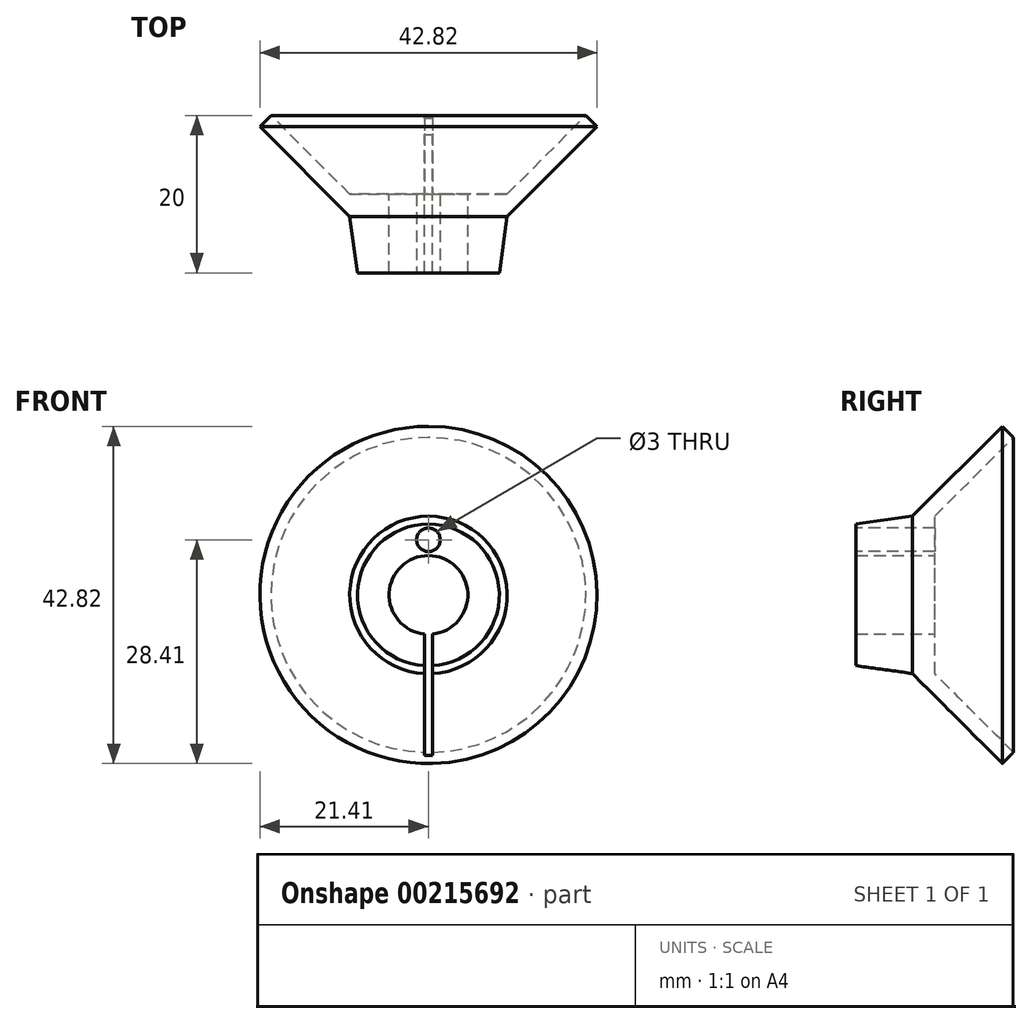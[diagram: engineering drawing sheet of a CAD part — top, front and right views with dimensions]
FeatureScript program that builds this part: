
annotation { "Feature Type Name" : "Feature", "Feature Type Description" : "" }
export const myFeature = defineFeature(function(context is Context, id is Id, definition is map)
    precondition{}
    {
        {
            var Q0;
            Q0=qCreatedBy(makeId("Top.planeOp"),FACE);
            var sketch = newSketch(context, id + "F0", { "sketchPlane" : qUnion([Q0])});
            skLineSegment(sketch, "E0", {"start": v(0, 36.3) * mm, "end": v(0, -39) * mm, "construction": true});
            skLineSegment(sketch, "E1", {"start": v(-20, 20) * mm, "end": v(-21.41, 18.59) * mm});
            skLineSegment(sketch, "E2", {"start": v(-21.41, 18.59) * mm, "end": v(-10, 7.17) * mm});
            skLineSegment(sketch, "E3", {"start": v(-5, 0) * mm, "end": v(-5, 10) * mm});
            skLineSegment(sketch, "E4", {"start": v(-10, 7.17) * mm, "end": v(-9, 0) * mm});
            skLineSegment(sketch, "E5", {"start": v(-9, 0) * mm, "end": v(-5, 0) * mm});
            skLineSegment(sketch, "E6", {"start": v(-5, 10) * mm, "end": v(-10, 10) * mm});
            skLineSegment(sketch, "E7", {"start": v(-10, 10) * mm, "end": v(-20, 20) * mm});
            skSolve(sketch);
        }
        {
            var Q0;
            Q0 = qSketchRegion(id + "F0", true);
            var Q1;
            Q1=sQuery(id+"F0.wireOp",EDGE,"E0");
            revolve(context, id + "F1", {"entities" : qUnion([Q0]), "axis" : qUnion([Q1]), "revolveType" : RevolveType.FULL});
        }
        {
            var Q0;
            Q0=makeQuery(id+"F1.opRevolve","SWEPT_FACE",FACE,{"disambiguationData":[OSD([sQuery(id+"F0.wireOp",EDGE,"E5")])]});
            var sketch = newSketch(context, id + "F2", { "sketchPlane" : qUnion([Q0])});
            skLineSegment(sketch, "E8", {"start": v(0, 9) * mm, "end": v(0, 5) * mm, "construction": true});
            skCircle(sketch, "E9", {"center": v(0, 7) * mm, "radius": 1.5 * mm});
            skSolve(sketch);
        }
        {
            var Q0;
            Q0 = qSketchRegion(id + "F2", true);
            extrude(context, id + "F3", {"entities" : qUnion([Q0]), "operationType" : NewBodyOperationType.REMOVE, "endBound" : BoundingType.THROUGH_ALL, "oppositeDirection" : true, "depth" : 25 * mm});
        }
        {
            var Q0;
            Q0=makeQuery(id+"F1.opRevolve","SWEPT_FACE",FACE,{"disambiguationData":[OSD([sQuery(id+"F0.wireOp",EDGE,"E5")])]});
            var sketch = newSketch(context, id + "F4", { "sketchPlane" : qUnion([Q0])});
            skLineSegment(sketch, "E10.bottom", {"start": v(-0.5, 0) * mm, "end": v(0.5, 0) * mm});
            skLineSegment(sketch, "E10.top", {"start": v(-0.5, -20.4) * mm, "end": v(0.5, -20.4) * mm});
            skLineSegment(sketch, "E10.left", {"start": v(-0.5, 0) * mm, "end": v(-0.5, -20.4) * mm});
            skLineSegment(sketch, "E10.right", {"start": v(0.5, 0) * mm, "end": v(0.5, -20.4) * mm});
            skSolve(sketch);
        }
        {
            var Q0;
            Q0 = qSketchRegion(id + "F4", true);
            extrude(context, id + "F5", {"entities" : qUnion([Q0]), "operationType" : NewBodyOperationType.REMOVE, "oppositeDirection" : true, "depth" : 25 * mm});
        }
    });
